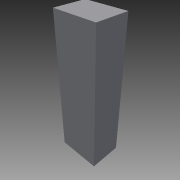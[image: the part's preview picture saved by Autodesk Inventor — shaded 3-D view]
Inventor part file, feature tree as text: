
AUTODESK INVENTOR PART (.ipt)
format: ipt  version: 2013 (Build 170138000, 138)  size: 65,536 bytes
history: native  units: in
note: dims shown in document units (in); Inventor stores cm internally (conversion verified against a paired STEP export)
features: reference x2, extrude x1, sketch x1
ambient origin geometry x8: Origin, YZ Plane, XZ Plane, XY Plane, X Axis, Y Axis, Z Axis, Center Point
bodies: Solid1 (feature_tree)
feature tree (4):
  extrude  "Extrusion1"  [1 undecoded]
  sketch  "Sketch1"  dims[d0=1.0in d1=0.0in]
  reference  "Reference1"
  reference  "Reference2"
note: 1 required parameter value undecoded (feature->parameter linkage not recoverable at this tier; creation-order binding heuristic only, values carry confidence <= 0.55)
